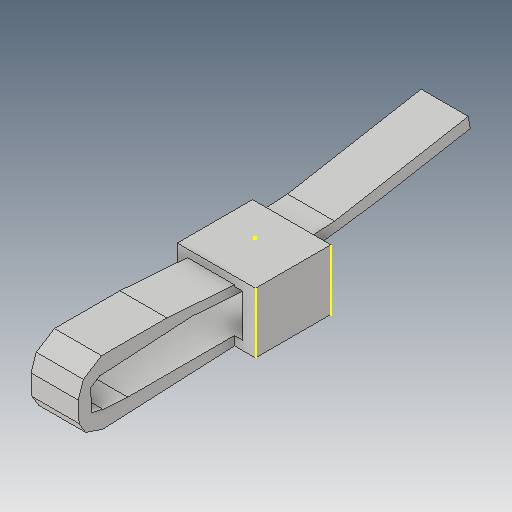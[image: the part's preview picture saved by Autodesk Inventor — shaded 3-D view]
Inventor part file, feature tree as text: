
AUTODESK INVENTOR PART (.ipt)
format: ipt  version: 2017 (Build 210142000, 142)  size: 150,528 bytes
history: native  units: mm
features: sketch x4, other x3
ambient origin geometry x8: Origin, YZ Plane, XZ Plane, XY Plane, X Axis, Y Axis, Z Axis, Center Point
bodies: Solid1 (feature_tree)
feature tree (7):
  other  "Ziptie.ipt"
  other  "Solid1::Ziptie.ipt"
  other  "TaggingFeature1"
  sketch  "Sketch1"  dims[d0=10.0mm]
  sketch  "Sketch3"
  sketch  "Sketch4"
  sketch  "Sketch5"
